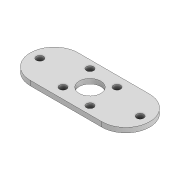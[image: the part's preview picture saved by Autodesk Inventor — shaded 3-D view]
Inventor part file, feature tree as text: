
AUTODESK INVENTOR PART (.ipt)
format: ipt  version: 2022 (Build 260153000, 153)  size: 138,240 bytes
history: native  units: mm
features: extrude x1, sketch x1, projected_geometry x1
ambient origin geometry x8: Origin, YZ Plane, XZ Plane, XY Plane, X Axis, Y Axis, Z Axis, Center Point
bodies: Body1 (feature_tree)
feature tree (3):
  extrude  "Extrusion2"  Depth=20.0mm
  sketch  "Sketch3"  dims[d37=3.0mm d38=3.0mm d39=3.0mm d40=3.0mm d41=9.5mm d42=9.5mm d43=8.0mm d44=8.0mm d55=2.0mm d56=0.0mm d60=20.0mm d61=9.0mm d66=5.0mm d67=5.0mm d68=3.0mm d69=3.0mm d70=6.0mm d71=6.0mm]
  projected_geometry  "Projected Loop1"
